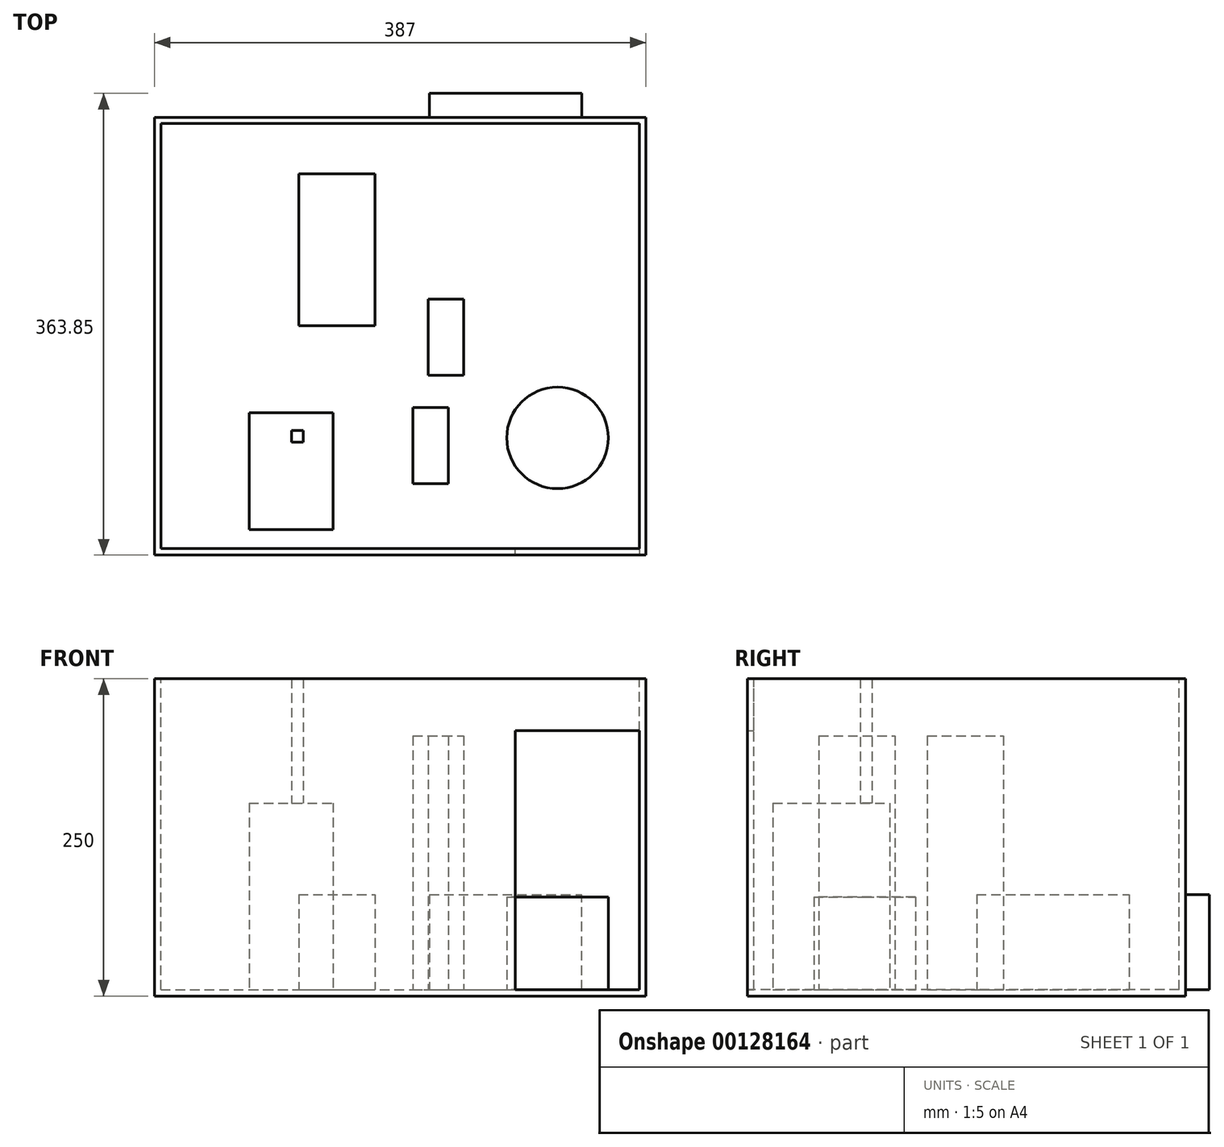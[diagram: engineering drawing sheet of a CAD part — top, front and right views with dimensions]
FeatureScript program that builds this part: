
annotation { "Feature Type Name" : "Feature", "Feature Type Description" : "" }
export const myFeature = defineFeature(function(context is Context, id is Id, definition is map)
    precondition{}
    {
        {
            var Q0;
            Q0=qCreatedBy(makeId("Top.planeOp"),FACE);
            var sketch = newSketch(context, id + "F0", { "sketchPlane" : qUnion([Q0])});
            skLineSegment(sketch, "E0.bottom", {"start": v(-387, 345) * mm, "end": v(0, 345) * mm});
            skLineSegment(sketch, "E0.top", {"start": v(-387, 0) * mm, "end": v(0, 0) * mm});
            skLineSegment(sketch, "E0.left", {"start": v(-387, 345) * mm, "end": v(-387, 0) * mm});
            skLineSegment(sketch, "E0.right", {"start": v(0, 345) * mm, "end": v(0, 0) * mm});
            skSolve(sketch);
        }
        {
            var Q0;
            Q0 = qSketchRegion(id + "F0", true);
            extrude(context, id + "F1", {"entities" : qUnion([Q0]), "depth" : 250 * mm});
        }
        {
            var Q0;
            Q0=makeQuery(id+"F1.opExtrude","CAP_FACE",FACE,{"disambiguationData":[OSD([sQuery(id+"F0.wireOp",EDGE,"E0.bottom"),sQuery(id+"F0.wireOp",EDGE,"E0.top"),sQuery(id+"F0.wireOp",EDGE,"E0.left"),sQuery(id+"F0.wireOp",EDGE,"E0.right")])],"isStart":false});
            var sketch = newSketch(context, id + "F2", { "sketchPlane" : qUnion([Q0])});
            skLineSegment(sketch, "E1.bottom", {"start": v(-382, 340) * mm, "end": v(-5, 340) * mm});
            skLineSegment(sketch, "E1.top", {"start": v(-382, 5) * mm, "end": v(-5, 5) * mm});
            skLineSegment(sketch, "E1.left", {"start": v(-382, 340) * mm, "end": v(-382, 5) * mm});
            skLineSegment(sketch, "E1.right", {"start": v(-5, 340) * mm, "end": v(-5, 5) * mm});
            skSolve(sketch);
        }
        {
            var Q0;
            Q0 = qSketchRegion(id + "F2", true);
            extrude(context, id + "F3", {"entities" : qUnion([Q0]), "operationType" : NewBodyOperationType.REMOVE, "oppositeDirection" : true, "depth" : 245 * mm});
        }
        {
            var Q0;
            Q0=makeQuery(id+"F3.boolean.opBoolean","COPY",FACE,{"derivedFrom":makeQuery(id+"F3.opExtrude","SWEPT_FACE",FACE,{"disambiguationData":[OSD([sQuery(id+"F2.wireOp",EDGE,"E1.top")])]})});
            var sketch = newSketch(context, id + "F4", { "sketchPlane" : qUnion([Q0])});
            skLineSegment(sketch, "E2.bottom", {"start": v(5, 5) * mm, "end": v(103, 5) * mm});
            skLineSegment(sketch, "E2.top", {"start": v(5, 209) * mm, "end": v(103, 209) * mm});
            skLineSegment(sketch, "E2.left", {"start": v(5, 5) * mm, "end": v(5, 209) * mm});
            skLineSegment(sketch, "E2.right", {"start": v(103, 5) * mm, "end": v(103, 209) * mm});
            skSolve(sketch);
        }
        {
            var Q0;
            Q0 = qSketchRegion(id + "F4", true);
            extrude(context, id + "F5", {"entities" : qUnion([Q0]), "operationType" : NewBodyOperationType.REMOVE, "oppositeDirection" : true, "depth" : 25 * mm});
        }
        {
            var Q0;
            Q0=makeQuery(id+"F5.boolean.opBoolean","MERGE",FACE,{"derivedFrom":[makeQuery(id+"F3.boolean.opBoolean","COPY",FACE,{"derivedFrom":makeQuery(id+"F3.opExtrude","CAP_FACE",FACE,{"disambiguationData":[OSD([sQuery(id+"F2.wireOp",EDGE,"E1.bottom"),sQuery(id+"F2.wireOp",EDGE,"E1.top"),sQuery(id+"F2.wireOp",EDGE,"E1.left"),sQuery(id+"F2.wireOp",EDGE,"E1.right")])],"isStart":false})}),makeQuery(id+"F5.opExtrude","SWEPT_FACE",FACE,{"disambiguationData":[OSD([sQuery(id+"F4.wireOp",EDGE,"E2.bottom")])]})]});
            var sketch = newSketch(context, id + "F6", { "sketchPlane" : qUnion([Q0])});
            skLineSegment(sketch, "E3.bottom", {"start": v(-279, 98) * mm, "end": v(-270, 98) * mm});
            skLineSegment(sketch, "E3.top", {"start": v(-279, 89) * mm, "end": v(-270, 89) * mm});
            skLineSegment(sketch, "E3.left", {"start": v(-279, 98) * mm, "end": v(-279, 89) * mm});
            skLineSegment(sketch, "E3.right", {"start": v(-270, 98) * mm, "end": v(-270, 89) * mm});
            skSolve(sketch);
        }
        {
            var Q0;
            Q0 = qSketchRegion(id + "F6", true);
            extrude(context, id + "F7", {"entities" : qUnion([Q0]), "operationType" : NewBodyOperationType.ADD, "depth" : 245 * mm});
        }
        {
            var Q0;
            Q0=makeQuery(id+"F5.boolean.opBoolean","MERGE",FACE,{"derivedFrom":[makeQuery(id+"F3.boolean.opBoolean","COPY",FACE,{"derivedFrom":makeQuery(id+"F3.opExtrude","CAP_FACE",FACE,{"disambiguationData":[OSD([sQuery(id+"F2.wireOp",EDGE,"E1.bottom"),sQuery(id+"F2.wireOp",EDGE,"E1.top"),sQuery(id+"F2.wireOp",EDGE,"E1.left"),sQuery(id+"F2.wireOp",EDGE,"E1.right")])],"isStart":false})}),makeQuery(id+"F5.opExtrude","SWEPT_FACE",FACE,{"disambiguationData":[OSD([sQuery(id+"F4.wireOp",EDGE,"E2.bottom")])]})]});
            var sketch = newSketch(context, id + "F8", { "sketchPlane" : qUnion([Q0])});
            skLineSegment(sketch, "E4.bottom", {"start": v(-273.49, 180.55) * mm, "end": v(-213.49, 180.55) * mm});
            skLineSegment(sketch, "E4.top", {"start": v(-273.49, 300.55) * mm, "end": v(-213.49, 300.55) * mm});
            skLineSegment(sketch, "E4.left", {"start": v(-273.49, 180.55) * mm, "end": v(-273.49, 300.55) * mm});
            skLineSegment(sketch, "E4.right", {"start": v(-213.49, 180.55) * mm, "end": v(-213.49, 300.55) * mm});
            skSolve(sketch);
        }
        {
            var Q0;
            Q0 = qSketchRegion(id + "F8", true);
            extrude(context, id + "F9", {"entities" : qUnion([Q0]), "operationType" : NewBodyOperationType.ADD, "depth" : 75 * mm});
        }
        {
            var Q0;
            Q0=makeQuery(id+"F5.boolean.opBoolean","MERGE",FACE,{"derivedFrom":[makeQuery(id+"F3.boolean.opBoolean","COPY",FACE,{"derivedFrom":makeQuery(id+"F3.opExtrude","CAP_FACE",FACE,{"disambiguationData":[OSD([sQuery(id+"F2.wireOp",EDGE,"E1.bottom"),sQuery(id+"F2.wireOp",EDGE,"E1.top"),sQuery(id+"F2.wireOp",EDGE,"E1.left"),sQuery(id+"F2.wireOp",EDGE,"E1.right")])],"isStart":false})}),makeQuery(id+"F5.opExtrude","SWEPT_FACE",FACE,{"disambiguationData":[OSD([sQuery(id+"F4.wireOp",EDGE,"E2.bottom")])]})]});
            var sketch = newSketch(context, id + "F10", { "sketchPlane" : qUnion([Q0])});
            skLineSegment(sketch, "E5", {"start": v(-50.35, 171.85) * mm, "end": v(-50.35, 363.85) * mm});
            skLineSegment(sketch, "E6", {"start": v(-50.35, 363.85) * mm, "end": v(-170.35, 363.85) * mm});
            skLineSegment(sketch, "E7", {"start": v(-170.35, 363.85) * mm, "end": v(-170.35, 303.85) * mm});
            skLineSegment(sketch, "E8", {"start": v(-170.35, 303.85) * mm, "end": v(-160.35, 303.85) * mm});
            skLineSegment(sketch, "E9", {"start": v(-130.35, 273.85) * mm, "end": v(-130.35, 199.55) * mm});
            skLineSegment(sketch, "E10", {"start": v(-50.35, 171.85) * mm, "end": v(-95.35, 171.85) * mm});
            skArc(sketch, "E11", {"start": v(-130.35, 199.55) * mm, "mid": v(-117.67, 179.61) * mm, "end": v(-95.35, 171.85) * mm});
            skPoint(sketch, "E12.visualSharp", {"position": v(-130.35, 303.85) * mm});
            skArc(sketch, "E12.filletArc", {"start": v(-130.35, 273.85) * mm, "mid": v(-139.13, 295.06) * mm, "end": v(-160.35, 303.85) * mm});
            skSolve(sketch);
        }
        {
            var Q0;
            Q0=makeQuery(id+"F10.imprint","IMPRINT",FACE,{"disambiguationData":[TD([[makeQuery(id+"F10.imprint","IMPRINT",EDGE,{"derivedFrom":sQuery(id+"F10.wireOp",EDGE,"E5")}),1.0]])]});
            extrude(context, id + "F11", {"entities" : qUnion([Q0]), "operationType" : NewBodyOperationType.ADD, "depth" : 75 * mm});
        }
        {
            var Q0;
            Q0=makeQuery(id+"F5.boolean.opBoolean","MERGE",FACE,{"derivedFrom":[makeQuery(id+"F3.boolean.opBoolean","COPY",FACE,{"derivedFrom":makeQuery(id+"F3.opExtrude","CAP_FACE",FACE,{"disambiguationData":[OSD([sQuery(id+"F2.wireOp",EDGE,"E1.bottom"),sQuery(id+"F2.wireOp",EDGE,"E1.top"),sQuery(id+"F2.wireOp",EDGE,"E1.left"),sQuery(id+"F2.wireOp",EDGE,"E1.right")])],"isStart":false})}),makeQuery(id+"F5.opExtrude","SWEPT_FACE",FACE,{"disambiguationData":[OSD([sQuery(id+"F4.wireOp",EDGE,"E2.bottom")])]})]});
            var sketch = newSketch(context, id + "F12", { "sketchPlane" : qUnion([Q0])});
            skLineSegment(sketch, "E13.bottom", {"start": v(-171.52, 141.65) * mm, "end": v(-143.52, 141.65) * mm});
            skLineSegment(sketch, "E13.top", {"start": v(-171.52, 201.65) * mm, "end": v(-143.52, 201.65) * mm});
            skLineSegment(sketch, "E13.left", {"start": v(-171.52, 141.65) * mm, "end": v(-171.52, 201.65) * mm});
            skLineSegment(sketch, "E13.right", {"start": v(-143.52, 141.65) * mm, "end": v(-143.52, 201.65) * mm});
            skSolve(sketch);
        }
        {
            var Q0;
            Q0=makeQuery(id+"F12.imprint","IMPRINT",FACE,{"disambiguationData":[TD([[makeQuery(id+"F12.imprint","IMPRINT",EDGE,{"derivedFrom":sQuery(id+"F12.wireOp",EDGE,"E13.bottom")}),1.0]])]});
            extrude(context, id + "F13", {"entities" : qUnion([Q0]), "depth" : 200 * mm});
        }
        {
            var Q0;
            Q0=makeQuery(id+"F5.boolean.opBoolean","MERGE",FACE,{"derivedFrom":[makeQuery(id+"F3.boolean.opBoolean","COPY",FACE,{"derivedFrom":makeQuery(id+"F3.opExtrude","CAP_FACE",FACE,{"disambiguationData":[OSD([sQuery(id+"F2.wireOp",EDGE,"E1.bottom"),sQuery(id+"F2.wireOp",EDGE,"E1.top"),sQuery(id+"F2.wireOp",EDGE,"E1.left"),sQuery(id+"F2.wireOp",EDGE,"E1.right")])],"isStart":false})}),makeQuery(id+"F5.opExtrude","SWEPT_FACE",FACE,{"disambiguationData":[OSD([sQuery(id+"F4.wireOp",EDGE,"E2.bottom")])]})]});
            var sketch = newSketch(context, id + "F14", { "sketchPlane" : qUnion([Q0])});
            skLineSegment(sketch, "E14.bottom", {"start": v(-183.5, 56.33) * mm, "end": v(-155.5, 56.33) * mm});
            skLineSegment(sketch, "E14.top", {"start": v(-183.5, 116.33) * mm, "end": v(-155.5, 116.33) * mm});
            skLineSegment(sketch, "E14.left", {"start": v(-183.5, 56.33) * mm, "end": v(-183.5, 116.33) * mm});
            skLineSegment(sketch, "E14.right", {"start": v(-155.5, 56.33) * mm, "end": v(-155.5, 116.33) * mm});
            skSolve(sketch);
        }
        {
            var Q0;
            Q0 = qSketchRegion(id + "F14", true);
            extrude(context, id + "F15", {"entities" : qUnion([Q0]), "operationType" : NewBodyOperationType.ADD, "depth" : 200 * mm});
        }
        {
            var Q0;
            Q0=makeQuery(id+"F5.boolean.opBoolean","MERGE",FACE,{"derivedFrom":[makeQuery(id+"F3.boolean.opBoolean","COPY",FACE,{"derivedFrom":makeQuery(id+"F3.opExtrude","CAP_FACE",FACE,{"disambiguationData":[OSD([sQuery(id+"F2.wireOp",EDGE,"E1.bottom"),sQuery(id+"F2.wireOp",EDGE,"E1.top"),sQuery(id+"F2.wireOp",EDGE,"E1.left"),sQuery(id+"F2.wireOp",EDGE,"E1.right")])],"isStart":false})}),makeQuery(id+"F5.opExtrude","SWEPT_FACE",FACE,{"disambiguationData":[OSD([sQuery(id+"F4.wireOp",EDGE,"E2.bottom")])]})]});
            var sketch = newSketch(context, id + "F16", { "sketchPlane" : qUnion([Q0])});
            skCircle(sketch, "E15", {"center": v(-69.55, 92.3) * mm, "radius": 40 * mm});
            skSolve(sketch);
        }
        {
            var Q0;
            Q0=makeQuery(id+"F16.imprint","IMPRINT",FACE,{"disambiguationData":[TD([[makeQuery(id+"F16.imprint","IMPRINT",EDGE,{"derivedFrom":sQuery(id+"F16.wireOp",EDGE,"E15")}),1.0]])]});
            extrude(context, id + "F17", {"entities" : qUnion([Q0]), "operationType" : NewBodyOperationType.ADD, "depth" : 73 * mm});
        }
        {
            var Q0;
            Q0=makeQuery(id+"F5.boolean.opBoolean","MERGE",FACE,{"derivedFrom":[makeQuery(id+"F3.boolean.opBoolean","COPY",FACE,{"derivedFrom":makeQuery(id+"F3.opExtrude","CAP_FACE",FACE,{"disambiguationData":[OSD([sQuery(id+"F2.wireOp",EDGE,"E1.bottom"),sQuery(id+"F2.wireOp",EDGE,"E1.top"),sQuery(id+"F2.wireOp",EDGE,"E1.left"),sQuery(id+"F2.wireOp",EDGE,"E1.right")])],"isStart":false})}),makeQuery(id+"F5.opExtrude","SWEPT_FACE",FACE,{"disambiguationData":[OSD([sQuery(id+"F4.wireOp",EDGE,"E2.bottom")])]})]});
            var sketch = newSketch(context, id + "F18", { "sketchPlane" : qUnion([Q0])});
            skLineSegment(sketch, "E16.bottom", {"start": v(-312.46, 20.06) * mm, "end": v(-246.46, 20.06) * mm});
            skLineSegment(sketch, "E16.top", {"start": v(-312.46, 112.06) * mm, "end": v(-246.46, 112.06) * mm});
            skLineSegment(sketch, "E16.left", {"start": v(-312.46, 20.06) * mm, "end": v(-312.46, 112.06) * mm});
            skLineSegment(sketch, "E16.right", {"start": v(-246.46, 20.06) * mm, "end": v(-246.46, 112.06) * mm});
            skSolve(sketch);
        }
        {
            var Q0;
            Q0=makeQuery(id+"F18.imprint","IMPRINT",FACE,{"disambiguationData":[TD([[makeQuery(id+"F18.imprint","IMPRINT",EDGE,{"derivedFrom":sQuery(id+"F18.wireOp",EDGE,"E16.bottom")}),1.0]])]});
            extrude(context, id + "F19", {"entities" : qUnion([Q0]), "operationType" : NewBodyOperationType.ADD, "depth" : 147 * mm});
        }
    });
